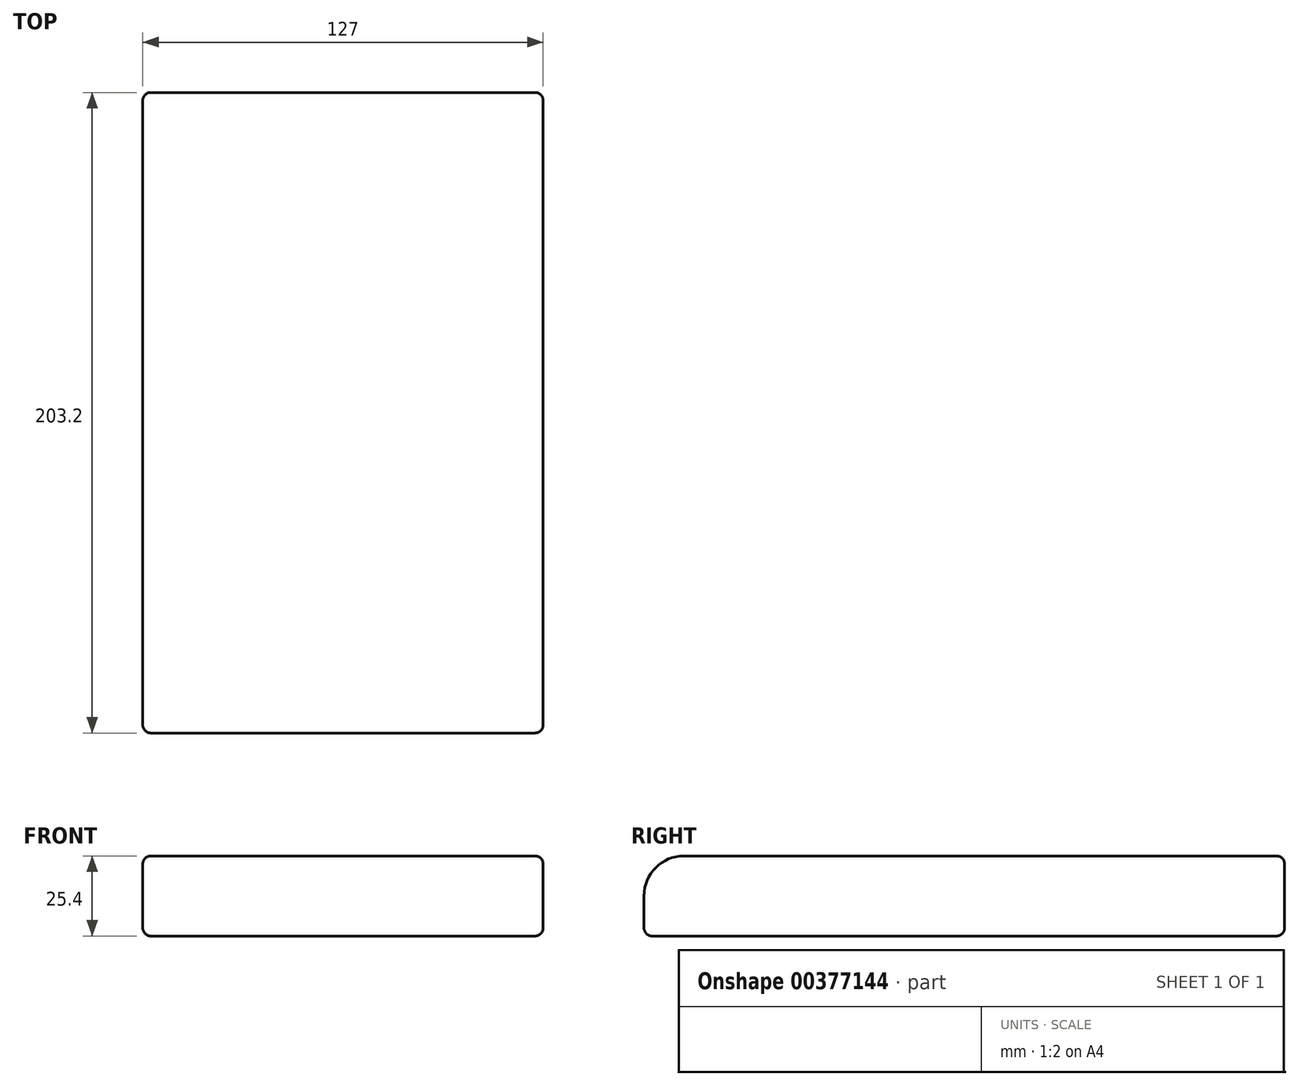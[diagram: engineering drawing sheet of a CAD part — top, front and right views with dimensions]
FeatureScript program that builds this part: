
annotation { "Feature Type Name" : "Feature", "Feature Type Description" : "" }
export const myFeature = defineFeature(function(context is Context, id is Id, definition is map)
    precondition{}
    {
        {
            var Q0;
            Q0=qCreatedBy(makeId("Top.planeOp"),FACE);
            var sketch = newSketch(context, id + "F0", { "sketchPlane" : qUnion([Q0])});
            skLineSegment(sketch, "E0.bottom", {"start": v(-63.5, 101.6) * mm, "end": v(63.5, 101.6) * mm});
            skLineSegment(sketch, "E0.top", {"start": v(-63.5, -101.6) * mm, "end": v(63.5, -101.6) * mm});
            skLineSegment(sketch, "E0.left", {"start": v(-63.5, 101.6) * mm, "end": v(-63.5, -101.6) * mm});
            skLineSegment(sketch, "E0.right", {"start": v(63.5, 101.6) * mm, "end": v(63.5, -101.6) * mm});
            skSolve(sketch);
        }
        {
            var Q0;
            Q0=makeQuery(id+"F0.imprint","IMPRINT",FACE,{"disambiguationData":[TD([[makeQuery(id+"F0.imprint","IMPRINT",EDGE,{"derivedFrom":sQuery(id+"F0.wireOp",EDGE,"E0.bottom")}),-1.0]])]});
            extrude(context, id + "F1", {"entities" : qUnion([Q0]), "depth" : 25.4 * mm});
        }
        {
            var Q0;
            Q0=makeQuery(id+"F1.opExtrude","CAP_EDGE",EDGE,{"disambiguationData":[OSD([sQuery(id+"F0.wireOp",EDGE,"E0.top")])],"isStart":false});
            fillet(context, id + "F2", {"entities" : qUnion([Q0]), "radius" : 12.7 * mm, "tangentPropagation" : true, "allowEdgeOverflow" : false});
        }
        {
            var Q0;
            Q0=makeQuery(id+"F1.opExtrude","CAP_EDGE",EDGE,{"disambiguationData":[OSD([sQuery(id+"F0.wireOp",EDGE,"E0.right")])],"isStart":false});
            var Q1;
            Q1=makeQuery(id+"F1.opExtrude","CAP_EDGE",EDGE,{"disambiguationData":[OSD([sQuery(id+"F0.wireOp",EDGE,"E0.right")])],"isStart":true});
            var Q2;
            Q2=makeQuery(id+"F1.opExtrude","CAP_EDGE",EDGE,{"disambiguationData":[OSD([sQuery(id+"F0.wireOp",EDGE,"E0.top")])],"isStart":true});
            var Q3;
            Q3=makeQuery(id+"F1.opExtrude","SWEPT_EDGE",EDGE,{"disambiguationData":[OSD([sQuery(id+"F0.wireOp",EDGE,"E0.bottom"),sQuery(id+"F0.wireOp",EDGE,"E0.right")])]});
            var Q4;
            Q4=makeQuery(id+"F1.opExtrude","CAP_EDGE",EDGE,{"disambiguationData":[OSD([sQuery(id+"F0.wireOp",EDGE,"E0.bottom")])],"isStart":false});
            var Q5;
            Q5=makeQuery(id+"F1.opExtrude","CAP_EDGE",EDGE,{"disambiguationData":[OSD([sQuery(id+"F0.wireOp",EDGE,"E0.bottom")])],"isStart":true});
            var Q6;
            Q6=makeQuery(id+"F1.opExtrude","SWEPT_EDGE",EDGE,{"disambiguationData":[OSD([sQuery(id+"F0.wireOp",EDGE,"E0.bottom"),sQuery(id+"F0.wireOp",EDGE,"E0.left")])]});
            var Q7;
            Q7=makeQuery(id+"F1.opExtrude","CAP_EDGE",EDGE,{"disambiguationData":[OSD([sQuery(id+"F0.wireOp",EDGE,"E0.left")])],"isStart":false});
            var Q8;
            Q8=makeQuery(id+"F1.opExtrude","CAP_EDGE",EDGE,{"disambiguationData":[OSD([sQuery(id+"F0.wireOp",EDGE,"E0.left")])],"isStart":true});
            fillet(context, id + "F3", {"entities" : qUnion([Q0, Q1, Q2, Q3, Q4, Q5, Q6, Q7, Q8]), "radius" : 2.54 * mm, "tangentPropagation" : true, "allowEdgeOverflow" : false});
        }
    });
